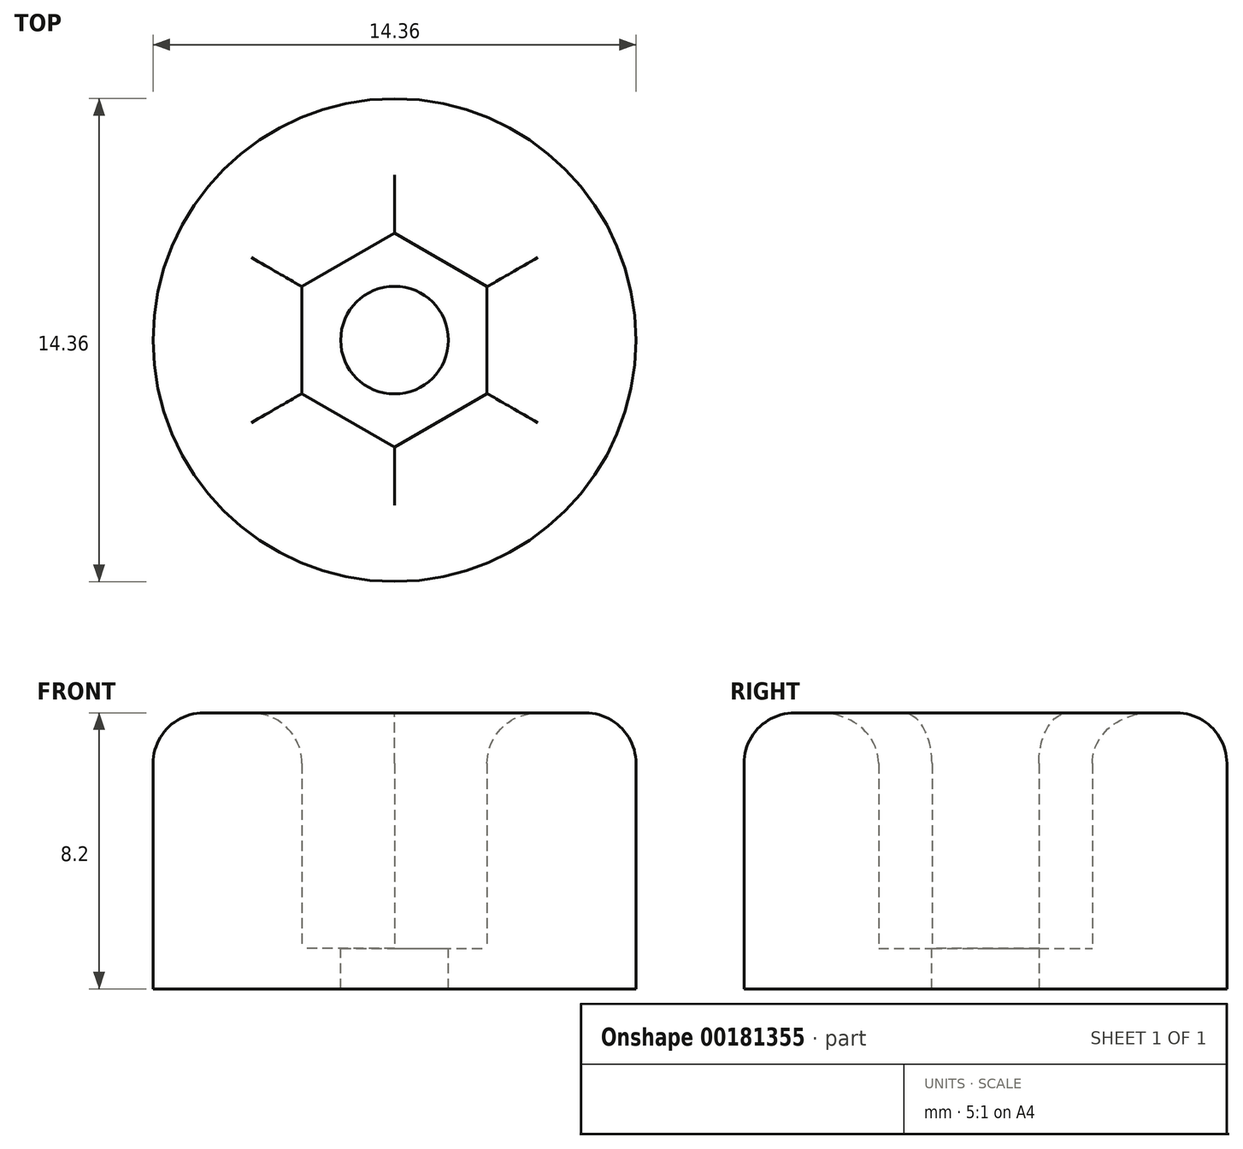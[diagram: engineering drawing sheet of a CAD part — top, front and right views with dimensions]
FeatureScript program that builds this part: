
annotation { "Feature Type Name" : "Feature", "Feature Type Description" : "" }
export const myFeature = defineFeature(function(context is Context, id is Id, definition is map)
    precondition{}
    {
        {
            var Q0;
            Q0=qCreatedBy(makeId("Top.planeOp"),FACE);
            var sketch = newSketch(context, id + "F0", { "sketchPlane" : qUnion([Q0])});
            skCircle(sketch, "E0.cCircle", {"center": v(0, 0) * mm, "radius": 2.75 * mm, "construction": true});
            skLineSegment(sketch, "E0.0", {"start": v(-2.75, -1.59) * mm, "end": v(-2.75, 1.59) * mm});
            skLineSegment(sketch, "E0.1", {"start": v(-2.75, 1.59) * mm, "end": v(0, 3.18) * mm});
            skLineSegment(sketch, "E0.2", {"start": v(0, 3.18) * mm, "end": v(2.75, 1.59) * mm});
            skLineSegment(sketch, "E0.3", {"start": v(2.75, 1.59) * mm, "end": v(2.75, -1.59) * mm});
            skLineSegment(sketch, "E0.4", {"start": v(2.75, -1.59) * mm, "end": v(0, -3.18) * mm});
            skLineSegment(sketch, "E0.5", {"start": v(0, -3.18) * mm, "end": v(-2.75, -1.59) * mm});
            skPoint(sketch, "E0.0.midPoint", {"position": v(-2.75, 0) * mm});
            skCircle(sketch, "E1", {"center": v(0, 0) * mm, "radius": 7.18 * mm});
            skSolve(sketch);
        }
        {
            var Q0;
            Q0=makeQuery(id+"F0.imprint","IMPRINT",FACE,{"disambiguationData":[TD([[makeQuery(id+"F0.imprint","IMPRINT",EDGE,{"derivedFrom":sQuery(id+"F0.wireOp",EDGE,"E0.0")}),1.0]])]});
            extrude(context, id + "F1", {"entities" : qUnion([Q0]), "depth" : 7 * mm});
        }
        {
            var Q0;
            Q0=makeQuery(id+"F1.opExtrude","CAP_FACE",FACE,{"disambiguationData":[OSD([sQuery(id+"F0.wireOp",EDGE,"E0.0"),sQuery(id+"F0.wireOp",EDGE,"E0.1"),sQuery(id+"F0.wireOp",EDGE,"E0.2"),sQuery(id+"F0.wireOp",EDGE,"E0.3"),sQuery(id+"F0.wireOp",EDGE,"E0.4"),sQuery(id+"F0.wireOp",EDGE,"E0.5"),sQuery(id+"F0.wireOp",EDGE,"E1")])],"isStart":true});
            var sketch = newSketch(context, id + "F2", { "sketchPlane" : qUnion([Q0])});
            skCircle(sketch, "E2", {"center": v(0, 0) * mm, "radius": 7.18 * mm});
            skCircle(sketch, "E3", {"center": v(0, 0) * mm, "radius": 1.6 * mm});
            skSolve(sketch);
        }
        {
            var Q0;
            Q0 = qSketchRegion(id + "F2", true);
            extrude(context, id + "F3", {"entities" : qUnion([Q0]), "operationType" : NewBodyOperationType.ADD, "depth" : 1.2 * mm});
        }
        {
            var Q0;
            Q0=makeQuery(id+"F1.opExtrude","CAP_FACE",FACE,{"disambiguationData":[OSD([sQuery(id+"F0.wireOp",EDGE,"E0.0"),sQuery(id+"F0.wireOp",EDGE,"E0.1"),sQuery(id+"F0.wireOp",EDGE,"E0.2"),sQuery(id+"F0.wireOp",EDGE,"E0.3"),sQuery(id+"F0.wireOp",EDGE,"E0.4"),sQuery(id+"F0.wireOp",EDGE,"E0.5"),sQuery(id+"F0.wireOp",EDGE,"E1")])],"isStart":false});
            fillet(context, id + "F4", {"entities" : qUnion([Q0]), "radius" : 1.5 * mm, "tangentPropagation" : true, "allowEdgeOverflow" : false});
        }
    });
